FCSTD DOCUMENT  (FreeCAD 0.16R6706 (Git))
Label: body
License: All rights reserved
LicenseURL: http://en.wikipedia.org/wiki/All_rights_reserved
objects: Sketcher::SketchObject×1
note: 1 computed .brp shape members not serialized (recipe doc carries the construction recipe); baked Part::Feature solids carry a one-line shape summary decoded from their .brp

FEATURE [Sketcher::SketchObject] Sketch  label="body"
  sketch-geometry (79):
    g0: LineSegment [constr] StartX=205.497 StartY=-9.11724 StartZ=0 EndX=205.497 EndY=-200.684 EndZ=0
    g1: GeomPoint [constr] X=205.497 Y=-104.901 Z=0
    g2: GeomPoint [constr] X=262.997 Y=-104.901 Z=0
    g3: LineSegment StartX=265.997 StartY=-99.0006 StartZ=0 EndX=288.497 EndY=-99.0006 EndZ=0
    g4: LineSegment StartX=288.497 StartY=-99.0006 StartZ=0 EndX=288.497 EndY=-110.801 EndZ=0
    g5: LineSegment StartX=288.497 StartY=-110.801 StartZ=0 EndX=265.997 EndY=-110.801 EndZ=0
    g6: LineSegment StartX=265.997 StartY=-110.801 StartZ=0 EndX=265.997 EndY=-99.0006 EndZ=0
    g7: Circle CenterX=291.497 CenterY=-104.901 CenterZ=0 NormalX=0 NormalY=0 NormalZ=1 Radius=1.2
    g8: Circle CenterX=262.997 CenterY=-104.901 CenterZ=0 NormalX=0 NormalY=0 NormalZ=1 Radius=1.2
    g9: GeomPoint [constr] X=282.597 Y=-104.901 Z=0
    g10: LineSegment [constr] StartX=128.397 StartY=-104.901 StartZ=0 EndX=282.597 EndY=-104.901 EndZ=0
    g11: GeomPoint [constr] X=147.997 Y=-104.901 Z=0
    g12: LineSegment StartX=144.997 StartY=-110.801 StartZ=0 EndX=122.497 EndY=-110.801 EndZ=0
    g13: LineSegment StartX=122.497 StartY=-110.801 StartZ=0 EndX=122.497 EndY=-99.0006 EndZ=0
    g14: LineSegment StartX=122.497 StartY=-99.0006 StartZ=0 EndX=144.997 EndY=-99.0006 EndZ=0
    g15: LineSegment StartX=144.997 StartY=-99.0006 StartZ=0 EndX=144.997 EndY=-110.801 EndZ=0
    g16: Circle CenterX=119.497 CenterY=-104.901 CenterZ=0 NormalX=0 NormalY=0 NormalZ=1 Radius=1.2
    g17: Circle CenterX=147.997 CenterY=-104.901 CenterZ=0 NormalX=0 NormalY=0 NormalZ=1 Radius=1.2
    g18: GeomPoint [constr] X=128.397 Y=-104.901 Z=0
    g19: GeomPoint [constr] X=205.497 Y=-36.0529 Z=0
    g20: GeomPoint [constr] X=205.497 Y=-173.748 Z=0
    g21: LineSegment [constr] StartX=205.497 StartY=-36.0529 StartZ=0 EndX=263.261 EndY=-9.11724 EndZ=0
    g22: LineSegment [constr] StartX=263.261 StartY=-9.11724 StartZ=0 EndX=147.733 EndY=-9.11724 EndZ=0
    g23: GeomPoint [constr] X=205.497 Y=-9.11724 Z=0
    g24: GeomPoint [constr] X=245.497 Y=-17.4006 Z=0
    g25: LineSegment StartX=245.723 StartY=-10.7855 StartZ=0 EndX=266.115 EndY=-1.27657 EndZ=0
    g26: LineSegment StartX=266.115 StartY=-1.27657 StartZ=0 EndX=271.101 EndY=-11.971 EndZ=0
    g27: LineSegment StartX=271.101 StartY=-11.971 StartZ=0 EndX=250.709 EndY=-21.4799 EndZ=0
    g28: LineSegment StartX=250.709 StartY=-21.4799 StartZ=0 EndX=245.723 EndY=-10.7855 EndZ=0
    g29: Circle CenterX=271.327 CenterY=-5.35594 CenterZ=0 NormalX=0 NormalY=0 NormalZ=1 Radius=1.2
    g30: Circle CenterX=245.497 CenterY=-17.4006 CenterZ=0 NormalX=0 NormalY=0 NormalZ=1 Radius=1.2
    g31: GeomPoint [constr] X=263.261 Y=-9.11724 Z=0
    g32: LineSegment [constr] StartX=205.497 StartY=-36.0529 StartZ=0 EndX=147.733 EndY=-9.11724 EndZ=0
    g33: GeomPoint [constr] X=165.497 Y=-17.4006 Z=0
    g34: LineSegment StartX=160.285 StartY=-21.4799 StartZ=0 EndX=139.893 EndY=-11.971 EndZ=0
    g35: LineSegment StartX=139.893 StartY=-11.971 StartZ=0 EndX=144.88 EndY=-1.27657 EndZ=0
    g36: LineSegment StartX=144.88 StartY=-1.27657 StartZ=0 EndX=165.272 EndY=-10.7855 EndZ=0
    g37: LineSegment StartX=165.272 StartY=-10.7855 StartZ=0 EndX=160.285 EndY=-21.4799 EndZ=0
    g38: Circle CenterX=139.667 CenterY=-5.35594 CenterZ=0 NormalX=0 NormalY=0 NormalZ=1 Radius=1.2
    g39: Circle CenterX=165.497 CenterY=-17.4006 CenterZ=0 NormalX=0 NormalY=0 NormalZ=1 Radius=1.2
    g40: GeomPoint [constr] X=147.733 Y=-9.11724 Z=0
    g41: LineSegment [constr] StartX=263.261 StartY=-9.11724 StartZ=0 EndX=263.261 EndY=-200.684 EndZ=0
    g42: GeomPoint [constr] X=263.261 Y=-104.901 Z=0
    g43: LineSegment [constr] StartX=205.497 StartY=-173.748 StartZ=0 EndX=263.261 EndY=-200.684 EndZ=0
    g44: LineSegment [constr] StartX=205.497 StartY=-173.748 StartZ=0 EndX=147.733 EndY=-200.684 EndZ=0
    g45: LineSegment StartX=271.101 StartY=-197.83 StartZ=0 EndX=266.115 EndY=-208.525 EndZ=0
    g46: Circle CenterX=271.327 CenterY=-204.445 CenterZ=0 NormalX=0 NormalY=0 NormalZ=1 Radius=1.2
    g47: GeomPoint [constr] X=263.261 Y=-200.684 Z=0
    g48: GeomPoint [constr] X=245.497 Y=-192.401 Z=0
    g49: LineSegment StartX=250.709 StartY=-188.321 StartZ=0 EndX=271.101 EndY=-197.83 EndZ=0
    g50: LineSegment StartX=266.115 StartY=-208.525 StartZ=0 EndX=245.723 EndY=-199.016 EndZ=0
    g51: LineSegment StartX=245.723 StartY=-199.016 StartZ=0 EndX=250.709 EndY=-188.321 EndZ=0
    g52: Circle CenterX=245.497 CenterY=-192.401 CenterZ=0 NormalX=0 NormalY=0 NormalZ=1 Radius=1.2
    g53: LineSegment StartX=144.88 StartY=-208.525 StartZ=0 EndX=139.893 EndY=-197.83 EndZ=0
    g54: Circle CenterX=139.667 CenterY=-204.445 CenterZ=0 NormalX=0 NormalY=0 NormalZ=1 Radius=1.2
    g55: GeomPoint [constr] X=147.733 Y=-200.684 Z=0
    g56: GeomPoint [constr] X=165.497 Y=-192.401 Z=0
    g57: LineSegment StartX=165.272 StartY=-199.016 StartZ=0 EndX=144.88 EndY=-208.525 EndZ=0
    g58: LineSegment StartX=139.893 StartY=-197.83 StartZ=0 EndX=160.285 EndY=-188.321 EndZ=0
    g59: LineSegment StartX=160.285 StartY=-188.321 StartZ=0 EndX=165.272 EndY=-199.016 EndZ=0
    g60: Circle CenterX=165.497 CenterY=-192.401 CenterZ=0 NormalX=0 NormalY=0 NormalZ=1 Radius=1.2
    g61: ArcOfCircle CenterX=263.261 CenterY=-9.11724 CenterZ=0 NormalX=0 NormalY=0 NormalZ=1 Radius=13 StartAngle=5.14872 EndAngle=8.29031
    g62: ArcOfCircle CenterX=282.597 CenterY=-104.901 CenterZ=0 NormalX=0 NormalY=0 NormalZ=1 Radius=13 StartAngle=4.71239 EndAngle=7.85398
    g63: LineSegment [constr] StartX=257.767 StartY=2.66476 StartZ=0 EndX=268.755 EndY=-20.8992 EndZ=0
    g64: LineSegment [constr] StartX=282.597 StartY=-91.9006 StartZ=0 EndX=282.597 EndY=-117.901 EndZ=0
    g65: ArcOfCircle CenterX=263.261 CenterY=-200.684 CenterZ=0 NormalX=0 NormalY=0 NormalZ=1 Radius=13 StartAngle=4.27606 EndAngle=7.41765
    g66: LineSegment [constr] StartX=268.755 StartY=-188.902 StartZ=0 EndX=257.767 EndY=-212.466 EndZ=0
    g67: ArcOfCircle CenterX=147.733 CenterY=-200.684 CenterZ=0 NormalX=0 NormalY=0 NormalZ=1 Radius=13 StartAngle=2.00713 EndAngle=5.14872
    g68: ArcOfCircle CenterX=128.397 CenterY=-104.901 CenterZ=0 NormalX=0 NormalY=0 NormalZ=1 Radius=13 StartAngle=1.5708 EndAngle=4.71239
    g69: ArcOfCircle CenterX=147.733 CenterY=-9.11724 CenterZ=0 NormalX=0 NormalY=0 NormalZ=1 Radius=13 StartAngle=1.13446 EndAngle=4.27606
    g70: LineSegment [constr] StartX=142.239 StartY=-188.902 StartZ=0 EndX=153.228 EndY=-212.466 EndZ=0
    g71: LineSegment [constr] StartX=128.397 StartY=-91.9006 StartZ=0 EndX=128.397 EndY=-117.901 EndZ=0
    g72: LineSegment [constr] StartX=153.228 StartY=2.66476 StartZ=0 EndX=142.239 EndY=-20.8992 EndZ=0
    g73: ArcOfCircle CenterX=282.597 CenterY=-55.0506 CenterZ=0 NormalX=0 NormalY=0 NormalZ=1 Radius=36.85 StartAngle=1.95588 EndAngle=4.71239
    g74: ArcOfCircle CenterX=282.597 CenterY=-154.751 CenterZ=0 NormalX=0 NormalY=0 NormalZ=1 Radius=36.85 StartAngle=1.5708 EndAngle=4.3273
    g75: ArcOfCircle CenterX=128.397 CenterY=-154.751 CenterZ=0 NormalX=0 NormalY=0 NormalZ=1 Radius=36.85 StartAngle=5.09748 EndAngle=7.85398
    g76: ArcOfCircle CenterX=128.397 CenterY=-55.0506 CenterZ=0 NormalX=0 NormalY=0 NormalZ=1 Radius=36.85 StartAngle=4.71239 EndAngle=7.46889
    g77: ArcOfCircle CenterX=205.497 CenterY=-324.558 CenterZ=0 NormalX=0 NormalY=0 NormalZ=1 Radius=123.68 StartAngle=1.13446 EndAngle=2.00713
    g78: ArcOfCircle CenterX=205.497 CenterY=114.757 CenterZ=0 NormalX=0 NormalY=0 NormalZ=1 Radius=123.68 StartAngle=4.27606 EndAngle=5.14872
  constraints (201):
    c: Vertical(g0)
    c: Symmetric(g0,g0,g1)
    c: Coincident(g3,g4)
    c: Coincident(g4,g5)
    c: Coincident(g5,g6)
    c: Coincident(g6,g3)
    c: Distance(g4,g3) = 11.8
    c: Distance(g4,g6) = 22.5
    c: Perpendicular(g6,g3)
    c: Perpendicular(g6,g5)
    c: Perpendicular(g4,g5)
    c: Distance(g7,g4) = 3
    c: Distance(g7,g3) = 5.9
    c: Distance(g8,g3) = 5.9
    c: Distance(g8,g6) = 3
    c: Coincident(g2,g8)
    c: Distance(g9,g4) = 5.9
    c: Distance(g9,g3) = 5.9
    c: Horizontal(g10)
    c: Symmetric(g10,g10,g1)
    c: Coincident(g9,g10)
    c: PointOnObject(g2,g10)
    c: Coincident(g12,g13)
    c: Coincident(g13,g14)
    c: Coincident(g14,g15)
    c: Coincident(g15,g12)
    c: Distance(g13,g12) = 11.8
    c: Distance(g13,g15) = 22.5
    c: Perpendicular(g15,g12)
    c: Perpendicular(g15,g14)
    c: Perpendicular(g13,g14)
    c: Distance(g16,g13) = 3
    c: Distance(g16,g12) = 5.9
    c: Distance(g17,g12) = 5.9
    c: Distance(g17,g15) = 3
    c: Coincident(g11,g17)
    c: Distance(g18,g13) = 5.9
    c: Distance(g18,g12) = 5.9
    c: Coincident(g10,g18)
    c: PointOnObject(g11,g10)
    c: PointOnObject(g19,g0)
    c: Symmetric(g20,g19,g1)
    c: Coincident(g21,g19)
    c: Coincident(g22,g21)
    c: Horizontal(g22)
    c: PointOnObject(g23,g22)
    c: PointOnObject(g23,g0)
    c: Symmetric(g21,g22,g23)
    c: Coincident(g25,g26)
    c: Coincident(g26,g27)
    c: Coincident(g27,g28)
    c: Coincident(g28,g25)
    c: Distance(g26,g25) = 11.8
    c: Distance(g26,g28) = 22.5
    c: Perpendicular(g28,g25)
    c: Perpendicular(g28,g27)
    c: Perpendicular(g26,g27)
    c: Distance(g29,g26) = 3
    c: Distance(g29,g25) = 5.9
    c: Distance(g30,g25) = 5.9
    c: Distance(g30,g28) = 3
    c: Coincident(g24,g30)
    c: Distance(g31,g26) = 5.9
    c: Distance(g31,g25) = 5.9
    c: Coincident(g21,g31)
    c: PointOnObject(g24,g21)
    c: Coincident(g32,g19)
    c: Coincident(g32,g22)
    c: Coincident(g34,g35)
    c: Coincident(g35,g36)
    c: Coincident(g36,g37)
    c: Coincident(g37,g34)
    c: Distance(g35,g34) = 11.8
    c: Distance(g35,g37) = 22.5
    c: Perpendicular(g37,g34)
    c: Perpendicular(g37,g36)
    c: Perpendicular(g35,g36)
    c: Distance(g38,g35) = 3
    c: Distance(g38,g34) = 5.9
    c: Distance(g39,g34) = 5.9
    c: Distance(g39,g37) = 3
    c: Coincident(g33,g39)
    c: Distance(g40,g35) = 5.9
    c: Distance(g40,g34) = 5.9
    c: Coincident(g22,g40)
    c: PointOnObject(g33,g32)
    c: Vertical(g41)
    c: Coincident(g21,g41)
    c: PointOnObject(g42,g41)
    c: PointOnObject(g42,g10)
    c: Symmetric(g21,g41,g42)
    c: PointOnObject(g0,g22)
    c: Radius(g7) = 1.2
    c: Radius(g8) = 1.2
    c: Radius(g29) = 1.2
    c: Radius(g30) = 1.2
    c: Radius(g38) = 1.2
    c: Radius(g39) = 1.2
    c: Radius(g17) = 1.2
    c: Radius(g16) = 1.2
    c: Coincident(g43,g20)
    c: Coincident(g43,g41)
    c: Coincident(g44,g20)
    c: Symmetric(g41,g44,g0)
    c: Coincident(g49,g45)
    c: Coincident(g45,g50)
    c: Coincident(g50,g51)
    c: Coincident(g51,g49)
    c: Distance(g45,g49) = 11.8
    c: Distance(g45,g51) = 22.5
    c: Perpendicular(g51,g49)
    c: Perpendicular(g51,g50)
    c: Perpendicular(g45,g50)
    c: Distance(g46,g45) = 3
    c: Distance(g46,g49) = 5.9
    c: Distance(g52,g49) = 5.9
    c: Distance(g52,g51) = 3
    c: Coincident(g48,g52)
    c: Distance(g47,g45) = 5.9
    c: Distance(g47,g49) = 5.9
    c: Equal(g7,g46) = 1.2
    c: Equal(g8,g52) = 1.2
    c: Coincident(g41,g47)
    c: PointOnObject(g48,g43)
    c: Coincident(g57,g53)
    c: Coincident(g53,g58)
    c: Coincident(g58,g59)
    c: Coincident(g59,g57)
    c: Distance(g53,g57) = 11.8
    c: Distance(g53,g59) = 22.5
    c: Perpendicular(g59,g57)
    c: Perpendicular(g59,g58)
    c: Perpendicular(g53,g58)
    c: Distance(g54,g53) = 3
    c: Distance(g54,g57) = 5.9
    c: Distance(g60,g57) = 5.9
    c: Distance(g60,g59) = 3
    c: Coincident(g56,g60)
    c: Distance(g55,g53) = 5.9
    c: Distance(g55,g57) = 5.9
    c: Coincident(g44,g55)
    c: PointOnObject(g56,g44)
    c: Radius(g54) = 1.2
    c: Radius(g60) = 1.2
    c: Angle(g10,g21) = 0.436332
    c: Coincident(g61,g21)
    c: Radius(g61) = 13
    c: Coincident(g62,g9)
    c: Radius(g62) = 13
    c: DistanceX(g1) = 205.497
    c: Coincident(g63,g61)
    c: Coincident(g63,g61)
    c: PointOnObject(g21,g63)
    c: Perpendicular(g63,g21)
    c: Coincident(g64,g62)
    c: Coincident(g64,g62)
    c: PointOnObject(g9,g64)
    c: Perpendicular(g64,g10)
    c: Coincident(g65,g41)
    c: Radius(g65) = 13
    c: Coincident(g66,g65)
    c: Coincident(g66,g65)
    c: PointOnObject(g41,g66)
    c: Perpendicular(g66,g43)
    c: Coincident(g67,g44)
    c: Coincident(g68,g10)
    c: Coincident(g69,g22)
    c: Radius(g69) = 13
    c: Radius(g68) = 13
    c: Radius(g67) = 13
    c: Coincident(g70,g67)
    c: Coincident(g70,g67)
    c: PointOnObject(g44,g70)
    c: Perpendicular(g44,g70)
    c: Coincident(g71,g68)
    c: Coincident(g71,g68)
    c: PointOnObject(g10,g71)
    c: Perpendicular(g10,g71)
    c: Coincident(g72,g69)
    c: Coincident(g72,g69)
    c: PointOnObject(g22,g72)
    c: Perpendicular(g32,g72)
    c: Distance(g24,g48) = 175
    c: Distance(g24,g33) = 80
    c: Distance(g2,g11) = 115
    c: PointOnObject(g73,g64)
    c: Coincident(g62,g73)
    c: Coincident(g61,g73)
    c: PointOnObject(g74,g64)
    c: Coincident(g62,g74)
    c: Coincident(g65,g74)
    c: PointOnObject(g75,g71)
    c: Coincident(g68,g75)
    c: Coincident(g67,g75)
    c: PointOnObject(g76,g71)
    c: Coincident(g68,g76)
    c: Coincident(g69,g76)
    c: Tangent(g65,g77)
    c: Tangent(g77,g67)
    c: Coincident(g67,g77)
    c: Coincident(g65,g77)
